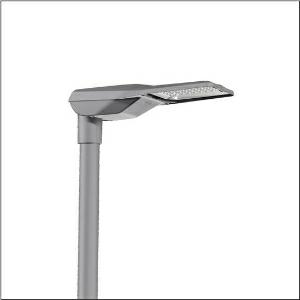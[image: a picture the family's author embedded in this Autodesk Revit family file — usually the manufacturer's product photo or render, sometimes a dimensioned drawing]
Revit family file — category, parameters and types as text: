
# Revit family: streetlight_sl_21_iq_mini___stw1_0a_5xe2e31d08jb_eadb
name_source: partatom
category: Lighting Fixtures
units: mm (PartAtom-declared; Revit-internal decimal feet)

## family parameters
Cut with Voids When Loaded = No
Host = Face
Light Source = No
Part Type = Normal
Room Calculation Point = No
Round Connector Dimension = Use Diameter
Shared = No

## types (1)
- --- (1 x LED, 10820 lm, 71.6 W, 3000K)
    Apparent Load = 72 VA
    CIE Flux Codes = 39 75 98 100 100
    Color Rendering = 70
    Color Temperature = 3000K
    Default Elevation = 1800 mm
    Description = Streetlight SL 21 iQ mini, mast luminaire, primary light control with lens, of PMMA, primary optical cover: cover, of toughened safety glass, transparent, light distribution: STW1.0a, light emission: direct distribution, primary light characteristic: asymmetric, installation type: post-top, side-entry, LED, High Power LED, rated luminous flux: 10.820lm, luminous efficacy: 151lm/W, light colour: 730, colour temperature: 3000K, control gear: iQ-Comfort, control: Auto-Match, Temp-Guard, Lumen-Switch, Night-Set, Smart-Wire, Light-Fading, Desk-Remote (wireless, voltage-free reading and setting of iQ features in the workshop via application-optimized NFC function/RFID function), optimised constant luminous flux control (CLO 2.0), pre-setting: linear dimming characteristic, mains connection: 220..240V, AC, 50/60Hz, start of lifetime: 72W, end of service life: 75W, reduction: 33W, luminaire housing, of diecast aluminium, powder-coated, Siteco® metallic grey (DB 702S), corrosivity category C5 mid according to DIN EN ISO 12944, please order mast flange separately, inclination adjustable: 0°, 5°, 10°, 15°, sealing non-destructively replaceable, multi-level sealing system, length: 628mm, width: 235mm, height: 110mm, mast flange for spigot size: 42mm (side-entry): 5XC10008XM4, 60/48mm (side-entry/post-top): 5XC10108XM2, 76/60mm (side-entry/post-top): 5XC10108XM1, mounting height: 4..8m, protection rating (complete): IP66, insulation class (complete): insulation class II (safety insulation), certification: CE, ENEC, ENEC+, VDE, impact resistance: IK10, permissible operating ambient temperature for outdoor applications: -40..+50°C, standard-compliant lighting for roads and squares, packaging unit: 1 piece

Light Distribution: STW1.0a
    Height = 110 mm
    Lamp = 1 x LED
    Lamp Light Flux = 10820 lm
    Lamp Power = 71.6 W
    Lamp count = 1
    Length = 625 mm
    Luminous efficacy = 151 lm/W
    Manufacturer = Siteco
    ModVariant = No
    Model = 5XE2E31D08JB
    Number of Poles = 1
    OnlyDefault = Yes
    Power Factor = 1
    Product Name = Streetlight SL 21 iQ mini | STW1.0a
    Product group = mast luminaire | pylon top
    ProductGroupID = 6100
    Protection Class = Protection class II
    Protection Degree = IP 66
    RLX_Detail_Level = 1
    RLX_Emergency_Light_Flux = 0 lm
    RLX_Emergency_Type = 0
    RLX_Emergency_Type_DB = No
    RlxData = <blob elided: 26349 chars, md5=fea7013a>
    Socket = socket
    Standby Power = 0 W
    System Light Flux = 10820 lm
    System Power = 72 W
    Type Comments = factory setting: luminous flux: 100 % | dim-lin: 254 | 746 mA
    Type Image = l_1003519.jpg
    URL = http://relux.com
    VarID = @adj_191699
    Voltage = 0 V
    Weight = 0.00 kg
    Width = 234 mm

## geometry (parser evidence)
native form markers: Blend x4, Sweep x10
no freeform markers — native parametric forms only
